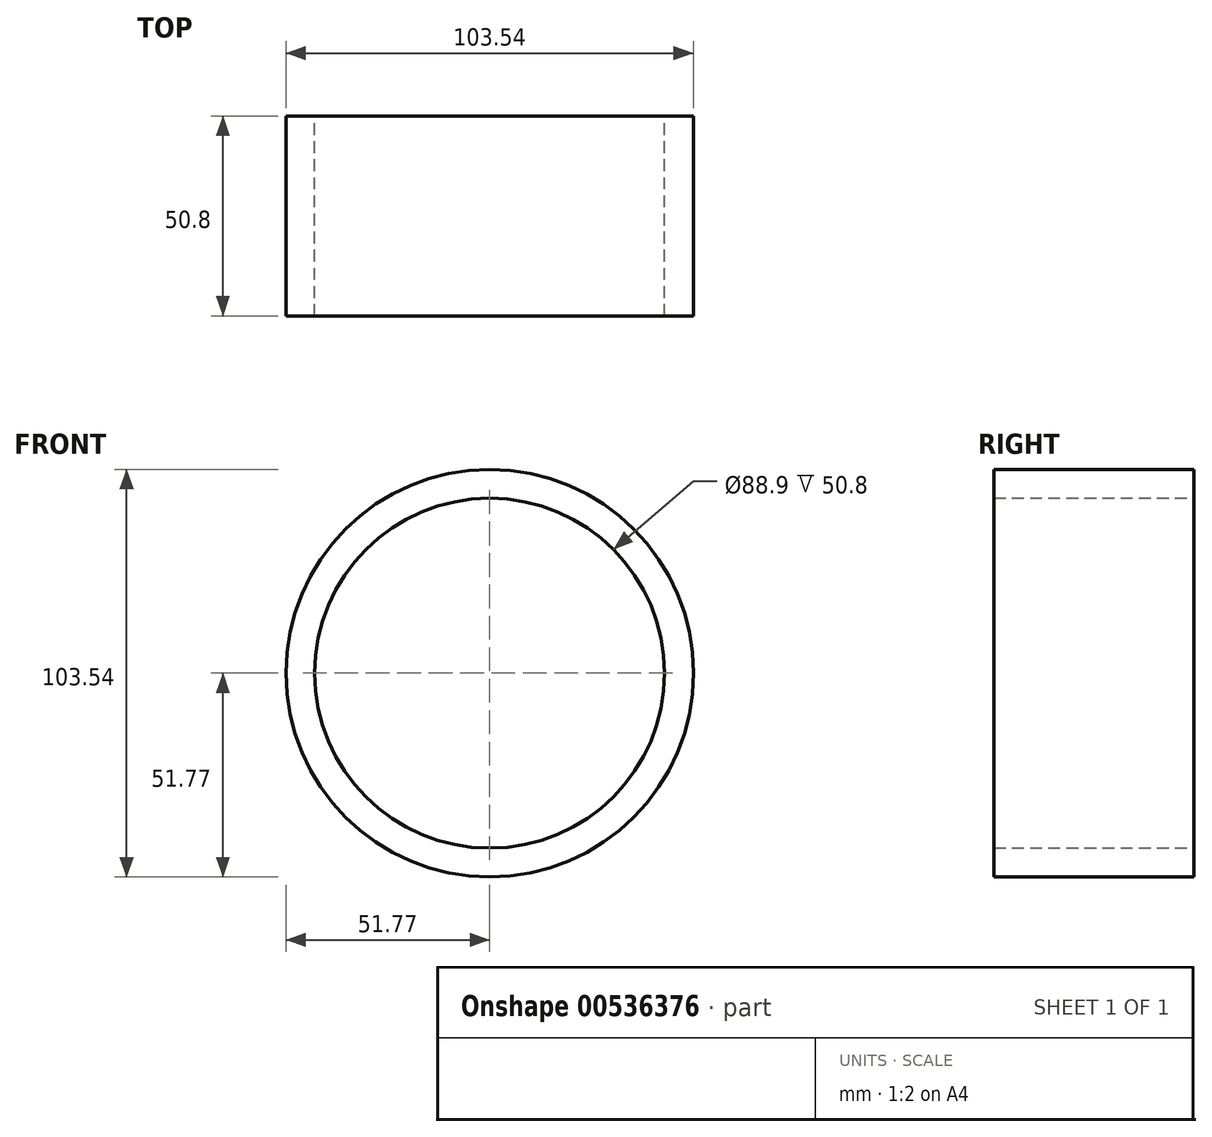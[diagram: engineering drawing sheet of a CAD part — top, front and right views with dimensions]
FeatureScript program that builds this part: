
annotation { "Feature Type Name" : "Feature", "Feature Type Description" : "" }
export const myFeature = defineFeature(function(context is Context, id is Id, definition is map)
    precondition{}
    {
        {
            var Q0;
            Q0=qCreatedBy(makeId("Front.planeOp"),FACE);
            var sketch = newSketch(context, id + "F0", { "sketchPlane" : qUnion([Q0])});
            skCircle(sketch, "E0", {"center": v(0, 0) * mm, "radius": 51.77 * mm});
            skSolve(sketch);
        }
        {
            var Q0;
            Q0 = qSketchRegion(id + "F0", true);
            extrude(context, id + "F1", {"entities" : qUnion([Q0]), "depth" : 50.8 * mm, "offsetDistance" : 25.4 * mm});
        }
        {
            var Q0;
            Q0=sQuery(id+"F0.wireOp",VERTEX,"E0.center");
            var Q1;
            Q1=makeQuery(id+"F1.opExtrude","SWEPT_BODY",BODY,{"disambiguationData":[OSD([sQuery(id+"F0.wireOp",EDGE,"E0")])]});
            hole(context, id + "F2", {"style" : HoleStyle.SIMPLE, "endStyle" : HoleEndStyle.THROUGH, "oppositeDirection" : true, "holeDiameter" : 88.9 * mm, "isTappedThrough" : true, "tappedDepth" : 12.7 * mm, "tapClearance" : 3, "locations" : qUnion([Q0]), "scope" : qUnion([Q1])});
        }
    });
